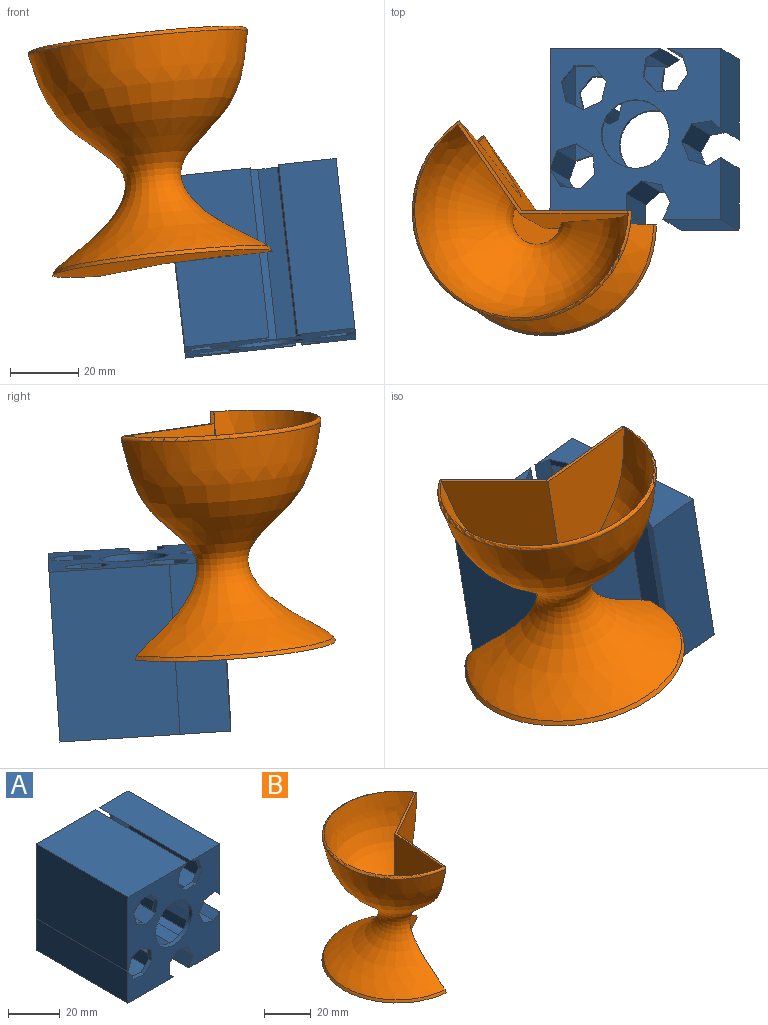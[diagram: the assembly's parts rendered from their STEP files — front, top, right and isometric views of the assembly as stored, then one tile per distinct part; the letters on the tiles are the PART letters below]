
ASSEMBLY  parts=2 mates=2
PART A: 84 faces, bbox 50x50x50 mm
  f0: plane 50x5.01mm, normal (0.85,0,0.52), area 199.9mm2, adj f1,f43,f44,f58,f59,f75,f82,f83
  f1: plane 5.83x2mm, normal (0.12,0,0.99), area 11.8mm2, adj f0,f2,f59,f83
  f2: plane 4.21x4.11mm, normal (-0.7,0,0.72), area 11.8mm2, adj f1,f3,f59,f83
  f3: plane 5.85x2mm, normal (-1,0,-0.1), area 11.8mm2, adj f2,f4,f59,f83
  f4: plane 4.94x3.19mm, normal (-0.54,0,-0.84), area 11.8mm2, adj f3,f5,f59,f83
  f5: plane 5.57x2mm, normal (0.32,0,-0.95), area 11.8mm2, adj f4,f6,f59,f83
  f6: plane 50x5.51mm, normal (0.94,0,-0.34), area 292.4mm2, adj f5,f38,f39,f58,f59,f74,f82,f83
  f7: plane 50x4.35mm, normal (0.51,0,-0.86), area 202.2mm2, adj f8,f36,f37,f58,f59,f73,f82,f83
  f8: plane 5.82x2mm, normal (0.99,0,-0.14), area 11.8mm2, adj f7,f9,f59,f83
  f9: plane 4.28x4.03mm, normal (0.73,0,0.68), area 11.8mm2, adj f8,f10,f59,f83
  f10: plane 5.86x2mm, normal (-0.08,0,1), area 11.8mm2, adj f9,f11,f59,f83
  f11: plane 4.88x3.28mm, normal (-0.83,0,0.56), area 11.8mm2, adj f10,f12,f59,f83
  f12: plane 50x5.61mm, normal (-0.95,0,-0.3), area 38.5mm2, adj f11,f32,f33,f58,f59,f72,f82,f83
  f13: plane 5.3x2.55mm, normal (0.43,0,0.9), area 11.8mm2, adj f18,f54,f59,f83
  f14: plane 5.73x2mm, normal (-0.97,0,0.22), area 11.8mm2, adj f15,f54,f59,f83
  f15: plane 4.6x3.67mm, normal (-0.78,0,-0.62), area 11.8mm2, adj f14,f16,f59,f83
  f16: plane 5.88x2mm, normal (0,0,-1), area 11.8mm2, adj f15,f17,f59,f83
  f17: plane 4.6x3.67mm, normal (0.78,0,-0.62), area 11.8mm2, adj f16,f18,f59,f83
  f18: plane 5.73x2mm, normal (0.97,0,0.22), area 11.8mm2, adj f13,f17,f59,f83
  f19: cylinder r=10mm len=20mm, axis (0,1,0), area 125.7mm2, adj f59,f83
  f20: plane 50x5.25mm, normal (-0.89,0,-0.45), area 294mm2, adj f21,f57,f58,f59
  f21: plane 50x4.85mm, normal (-0.91,0,0.42), area 266.6mm2, adj f20,f22,f58,f59
  f22: plane 50x16.86mm, normal (0,0,-1), area 843.1mm2, adj f21,f23,f58,f59
  f23: plane 50x18.08mm, normal (1,0,0), area 903.9mm2, adj f22,f24,f58,f59
  f24: plane 50x3.49mm, normal (-0.57,0,0.82), area 212.8mm2, adj f23,f25,f58,f59
  f25: plane 50x5.64mm, normal (0.28,0,0.96), area 294mm2, adj f24,f26,f58,f59
  f26: plane 50x5.45mm, normal (0.93,0,0.38), area 294mm2, adj f25,f27,f58,f59
  f27: plane 50x5.13mm, normal (0.87,0,-0.49), area 294mm2, adj f26,f28,f58,f59
  f28: plane 50x5.8mm, normal (0.16,0,-0.99), area 294mm2, adj f27,f29,f58,f59
  f29: plane 50x2.66mm, normal (-0.67,0,-0.74), area 179.6mm2, adj f28,f30,f58,f59
  f30: plane 50x23.59mm, normal (1,0,0), area 1179.4mm2, adj f29,f31,f58,f59
  f31: plane 50x15.75mm, normal (0,0,1), area 787.7mm2, adj f30,f32,f58,f59
  f32: plane 50x4.39mm, normal (-0.36,0,-0.93), area 235mm2, adj f12,f31,f58,f59
  f33: plane 4.88x3.28mm, normal (-0.83,0,0.56), area 11.8mm2, adj f12,f34,f58,f82
  f34: plane 5.86x2mm, normal (-0.08,0,1), area 11.8mm2, adj f33,f35,f58,f82
  f35: plane 4.28x4.03mm, normal (0.73,0,0.68), area 11.8mm2, adj f34,f36,f58,f82
  f36: plane 5.82x2mm, normal (0.99,0,-0.14), area 11.8mm2, adj f7,f35,f58,f82
  f37: plane 50x32.42mm, normal (0,0,1), area 1621.1mm2, adj f7,f38,f58,f59
  f38: plane 50x35.18mm, normal (-1,0,0), area 1759mm2, adj f6,f37,f58,f59
  f39: plane 5.57x2mm, normal (0.32,0,-0.95), area 11.8mm2, adj f6,f40,f58,f82
  f40: plane 4.94x3.19mm, normal (-0.54,0,-0.84), area 11.8mm2, adj f39,f41,f58,f82
  f41: plane 5.85x2mm, normal (-1,0,-0.1), area 11.8mm2, adj f40,f42,f58,f82
  f42: plane 4.21x4.11mm, normal (-0.7,0,0.72), area 11.8mm2, adj f41,f43,f58,f82
  f43: plane 5.83x2mm, normal (0.12,0,0.99), area 11.8mm2, adj f0,f42,f58,f82
  f44: plane 50x14.8mm, normal (-1,0,0), area 739.9mm2, adj f0,f45,f58,f59
  f45: plane 50x24.71mm, normal (0,0,-1), area 1235.5mm2, adj f44,f46,f58,f59
  f46: plane 50x2.17mm, normal (0.61,0,0.79), area 136.8mm2, adj f45,f47,f58,f59
  f47: plane 50x5.88mm, normal (1,0,0.02), area 294mm2, adj f46,f48,f58,f59
  f48: plane 50x4.53mm, normal (0.64,0,-0.77), area 294mm2, adj f47,f57,f58,f59
  f49: plane 5.73x2mm, normal (0.97,0,0.22), area 11.8mm2, adj f50,f55,f58,f82
  f50: plane 4.6x3.67mm, normal (0.78,0,-0.62), area 11.8mm2, adj f49,f51,f58,f82
  f51: plane 5.88x2mm, normal (0,0,-1), area 11.8mm2, adj f50,f52,f58,f82
  f52: plane 4.6x3.67mm, normal (-0.78,0,-0.62), area 11.8mm2, adj f51,f53,f58,f82
  f53: plane 5.73x2mm, normal (-0.97,0,0.22), area 11.8mm2, adj f52,f54,f58,f82
  f54: plane 50x5.3mm, normal (-0.43,0,0.9), area 294mm2, adj f13,f14,f53,f55,f58,f59,f60,f79
  f55: plane 5.3x2.55mm, normal (0.43,0,0.9), area 11.8mm2, adj f49,f54,f58,f82
  f56: cylinder r=10mm len=20mm, axis (0,1,0), area 125.7mm2, adj f58,f82
  f57: plane 50x5.76mm, normal (-0.2,0,-0.98), area 294mm2, adj f20,f48,f58,f59
  f58: plane 50x50mm, normal (0,-1,0), area 1578.3mm2, adj f0,f6,f7,f12,f20,f21,f22,f23
  f59: plane 50x50mm, normal (0,1,0), area 1578.3mm2, adj f0,f1,f2,f3,f4,f5,f6,f7
  f60: plane 46x2.3mm, normal (-0.43,0,-0.9), area 117.7mm2, adj f54,f80,f82,f83
  f61: plane 46x6.97mm, normal (0.89,0,0.45), area 359.1mm2, adj f62,f81,f82,f83
  f62: plane 46x2.89mm, normal (0.91,0,-0.42), area 146.1mm2, adj f61,f63,f82,f83
  f63: plane 46x11.74mm, normal (0,0,1), area 540.2mm2, adj f62,f64,f82,f83
  f64: plane 46x12.24mm, normal (-1,0,0), area 562.8mm2, adj f63,f65,f82,f83
  f65: plane 46x1.13mm, normal (0.57,0,-0.82), area 63.3mm2, adj f64,f66,f82,f83
  f66: plane 46x7.49mm, normal (-0.28,0,-0.96), area 359.1mm2, adj f65,f67,f82,f83
  f67: plane 46x7.23mm, normal (-0.93,0,-0.38), area 359.1mm2, adj f66,f68,f82,f83
  f68: plane 46x6.81mm, normal (-0.87,0,0.49), area 359.1mm2, adj f67,f69,f82,f83
  f69: plane 46x7.7mm, normal (-0.16,0,0.99), area 359.1mm2, adj f68,f70,f82,f83
  f70: plane 46x0.04mm, normal (0.67,0,0.74), area 2.2mm2, adj f69,f71,f82,f83
  f71: plane 46x17.08mm, normal (-1,0,0), area 785.7mm2, adj f70,f72,f82,f83
  f72: plane 46x9.27mm, normal (0,0,-1), area 426.4mm2, adj f12,f71,f82,f83
  f73: plane 46x27.01mm, normal (0,0,-1), area 1242.3mm2, adj f7,f74,f82,f83
  f74: plane 46x27.69mm, normal (1,0,0), area 1273.5mm2, adj f6,f73,f82,f83
  f75: plane 46x9.52mm, normal (1,0,0), area 438.1mm2, adj f0,f76,f82,f83
  f76: plane 46x18.53mm, normal (0,0,1), area 852.5mm2, adj f75,f77,f82,f83
  f77: plane 46x6.47mm, normal (-1,0,-0.02), area 297.6mm2, adj f76,f78,f82,f83
  f78: plane 46x6.01mm, normal (-0.64,0,0.77), area 359.1mm2, adj f77,f81,f82,f83
  f79: plane 46x2.49mm, normal (0.97,0,-0.22), area 117.7mm2, adj f54,f80,f82,f83
  f80: plane 46x2.42mm, normal (0.43,0,-0.9), area 123.7mm2, adj f60,f79,f82,f83
  f81: plane 46x7.64mm, normal (0.2,0,0.98), area 359.1mm2, adj f61,f78,f82,f83
  f82: plane 46x46mm, normal (0,1,0), area 1128.7mm2, adj f0,f6,f7,f12,f33,f34,f35,f36
  f83: plane 46x46mm, normal (0,-1,0), area 1128.7mm2, adj f0,f1,f2,f3,f4,f5,f6,f7
PART B: 11 faces, bbox 65x69.6x66.1 mm
  f0: plane 47.55x30.74mm, normal (0,0,1), area 62.9mm2, adj f4,f5,f8,f9,f10
  f1: cone r=0mm half-angle=89.7deg, axis (0,0,1), area 2143.3mm2, adj f2,f4,f5
  f2: cone r=32.33mm half-angle=30deg, axis (0,0,-1), area 182.1mm2, adj f1,f3,f4,f5
  f3: revolved ~64.25x63.5mm, area 6865.6mm2, adj f2,f4,f5,f10
  f4: plane 66.05x32.71mm, normal (1,-0.09,0), area 1371mm2, adj f0,f1,f2,f3,f5,f10
  f5: plane 66.05x28.52mm, normal (0.5,-0.87,0), area 1371mm2, adj f0,f1,f2,f3,f4,f10
  f6: cone r=0mm half-angle=89.7deg, axis (0,0,1), area 1829.8mm2, adj f7,f8,f9
  f7: revolved ~64.89x62.57mm, area 6449.6mm2, adj f6,f8,f9,f10
  f8: plane 65.05x31.78mm, normal (-1,0.09,0), area 1287.1mm2, adj f0,f6,f7,f9,f10
  f9: plane 65.05x27.63mm, normal (-0.5,0.87,0), area 1287.1mm2, adj f0,f6,f7,f8,f10
  f10: torus R=31.21mm, axis (0,0,-1), area 206.3mm2, adj f0,f3,f4,f5,f7,f8,f9
PLACE A rot(axis=(-1,-0.05,-0.05),93.8deg) t=(-71.34,-30.22,22.67)mm
PLACE B rot(axis=(-0.08,-0.02,1),95.2deg) t=(-77.89,-28.64,46.96)mm
MATE parallel A.f45 <-> B.f4  axis (0,-1,0.06) through (-61.84,-28.58,48.83)mm
MATE planar B.f4 <-> A.f45  axis (0,1,-0.06) through (-61.84,-28.58,48.83)mm
